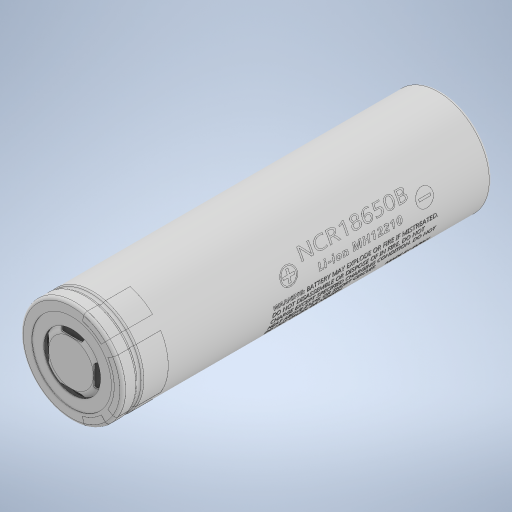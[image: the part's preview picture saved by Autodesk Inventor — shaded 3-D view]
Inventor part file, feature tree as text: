
AUTODESK INVENTOR PART (.ipt)
format: ipt  version: 2024 (Build 280153000, 153)  size: 12,069,376 bytes
history: native  units: mm
features: other x6, revolve x2
ambient origin geometry x8: Origin, YZ Plane, XZ Plane, XY Plane, X Axis, Y Axis, Z Axis, Center Point
bodies: Solide1 (feature_tree), Solide2 (feature_tree), Solide3 (feature_tree), Solide4 (feature_tree), Solide5 (feature_tree), Solide6 (feature_tree), Solide7 (feature_tree)
feature tree (8):
  other  "Bateria 18650 Panasonic.STEP"
  other  "Envolver1"
  revolve  "Revolución3"  [1 undecoded]
  revolve  "Revolución4"  [1 undecoded]
  other  "Cortar-Extruir1"
  other  "Cortar-Extruir3[1]"
  other  "Cortar-Extruir3[2]"
  other  "Cortar-Extruir3[3]"
note: 2 required parameter values undecoded (feature->parameter linkage not recoverable at this tier; creation-order binding heuristic only, values carry confidence <= 0.55)
